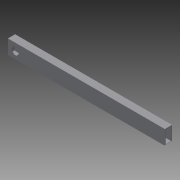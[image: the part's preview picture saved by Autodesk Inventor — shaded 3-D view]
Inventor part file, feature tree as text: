
AUTODESK INVENTOR PART (.ipt)
format: ipt  version: 2015 SP1 (Build 190203100, 203)  size: 136,192 bytes
history: native  units: in
note: dims shown in document units (in); Inventor stores cm internally (conversion verified against a paired STEP export)
features: sketch x3, hole x2, pattern_linear x2, extrude x1, fillet x1
ambient origin geometry x8: Origin, YZ Plane, XZ Plane, XY Plane, X Axis, Y Axis, Z Axis, Center Point
bodies: Solid1 (feature_tree)
feature tree (9):
  extrude  "Extrusion1"  Depth=1.0in
  fillet  "Fillet1"  Radius=1.75in
  hole  "Hole3"  [1 undecoded]
  pattern_linear  "Rectangular Pattern3"  Spacing1=21.75in  [1 undecoded]
  hole  "Hole4"  [1 undecoded]
  pattern_linear  "Rectangular Pattern4"  Spacing1=1.0in  [1 undecoded]
  sketch  "Sketch1"  dims[d0=2.0in d1=1.0in d2=1.75in]
  sketch  "Sketch4"  dims[d3=0.75in d4=0.125in]
  sketch  "Sketch5"  dims[d5=0.125in d6=21.75in d7=0.0in d32=0.125in d33=1.0in d34=3.0in d35=1.0in d36=0.75in d37=0.375in d38=0.25in d39=0.5635in d40=1.0in d41=0.8108in d42=1.9685in d44=1.5in d45=3.0in d46=1.0in d47=1.0in d48=0.75in d49=0.375in d50=0.25in d51=0.5635in d52=1.0in d53=0.8108in d54=1.9685in d56=1.5in]
note: 4 required parameter values undecoded (feature->parameter linkage not recoverable at this tier; creation-order binding heuristic only, values carry confidence <= 0.55)
